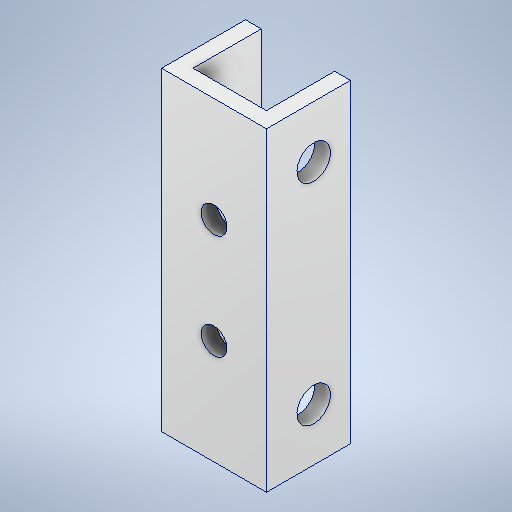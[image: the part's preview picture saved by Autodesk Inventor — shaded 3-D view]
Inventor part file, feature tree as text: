
AUTODESK INVENTOR PART (.ipt)
format: ipt  version: 2025 (Build 290162000, 162)  size: 282,112 bytes
history: native  units: mm
features: sketch x3, hole x2, other x1, extrude x1
ambient origin geometry x8: Origin, YZ Plane, XZ Plane, XY Plane, X Axis, Y Axis, Z Axis, Center Point
bodies: Body1 (feature_tree)
feature tree (7):
  other  "Těleso1"
  extrude  "Vysunutí1"  Depth=8.0mm
  hole  "Díra1"  [1 undecoded]
  hole  "Díra2"  [1 undecoded]
  sketch  "Náčrt1"
  sketch  "Náčrt2"
  sketch  "Náčrt3"
note: 2 required parameter values undecoded (feature->parameter linkage not recoverable at this tier; creation-order binding heuristic only, values carry confidence <= 0.55)
